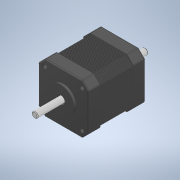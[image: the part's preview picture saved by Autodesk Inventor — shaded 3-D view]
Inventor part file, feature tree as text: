
AUTODESK INVENTOR PART (.ipt)
format: ipt  version: 2022 (Build 260153000, 153)  size: 742,400 bytes
history: mixed  units: in
note: dims shown in document units (in); Inventor stores cm internally (conversion verified against a paired STEP export)
features: sketch x5, extrude x1, chamfer x1, imported_body x1
ambient origin geometry x8: Origin, YZ Plane, XZ Plane, XY Plane, X Axis, Y Axis, Z Axis, Center Point
bodies: Solid1 (imported_parasolid), Body1 (imported_parasolid)
feature tree (8):
  sketch  "Sketch1"  dims[d0=0.1969in d1=0.8661in d2=0.0in d3=0.0197in d4=0.0787in d5=45.0deg]
  sketch  "Sketch2"
  sketch  "Sketch3"
  sketch  "Sketch4"
  extrude  "Extrusion1"  Depth=0.8661in TaperAngle=0.0deg
  chamfer  "Chamfer1"  Distance=0.0787in Angle=45.0deg
  sketch  "Sketch5"
  imported_body  NMx_Import_Brep_tag  [imported B-rep: ~20 faces, bbox_mm=[5.0, 31.0, 28.5]]
